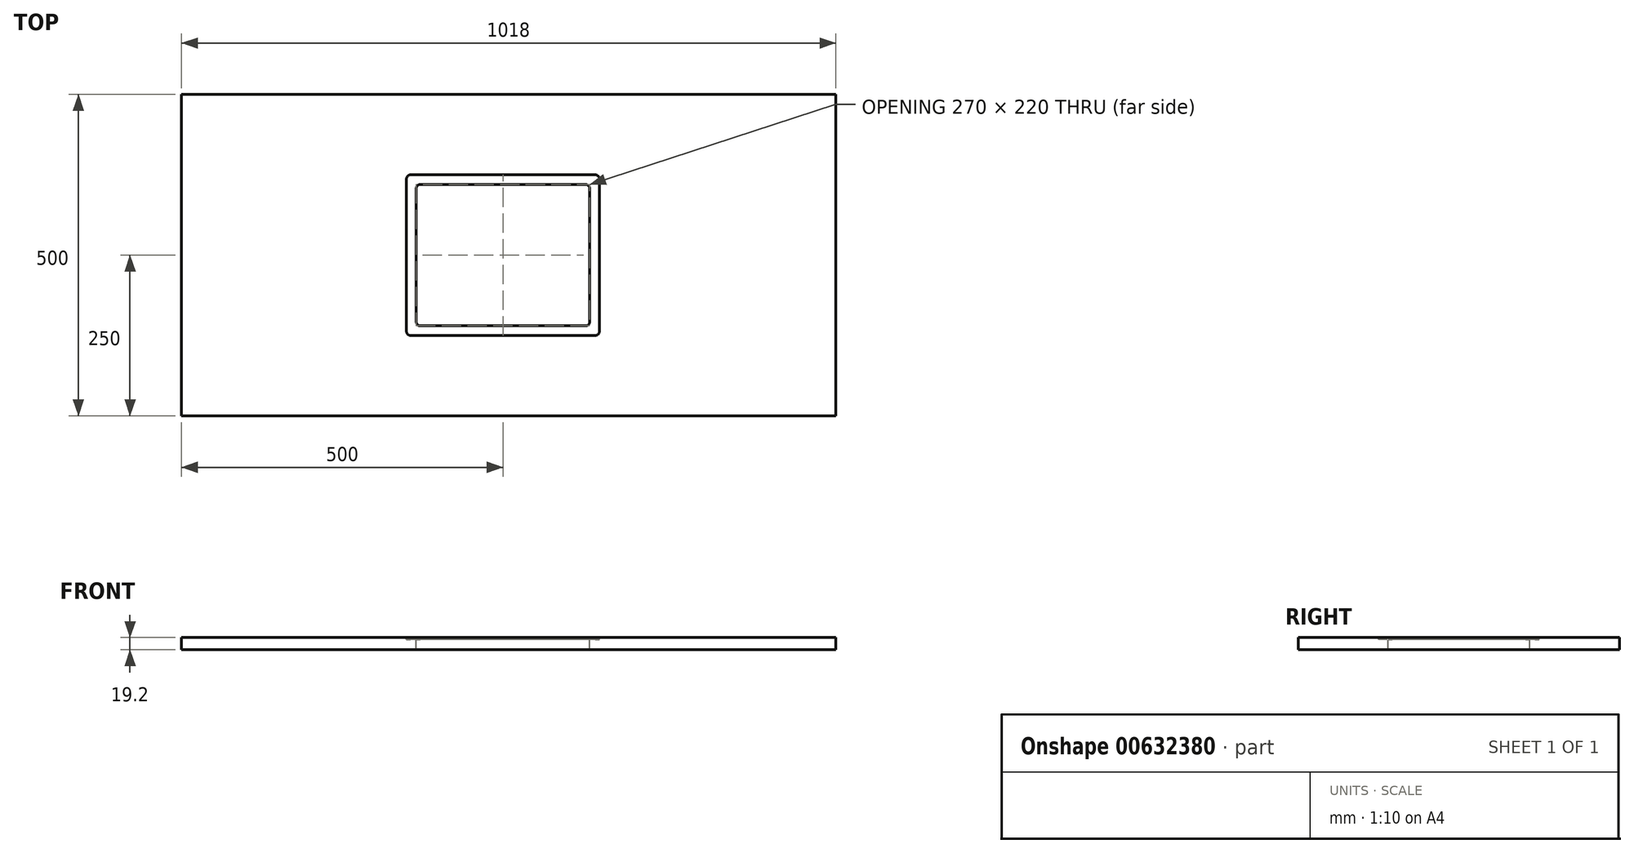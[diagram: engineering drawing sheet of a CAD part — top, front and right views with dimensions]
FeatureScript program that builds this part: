
annotation { "Feature Type Name" : "Feature", "Feature Type Description" : "" }
export const myFeature = defineFeature(function(context is Context, id is Id, definition is map)
    precondition{}
    {
        {
            var Q0;
            Q0=qCreatedBy(makeId("Top.planeOp"),FACE);
            var sketch = newSketch(context, id + "F0", { "sketchPlane" : qUnion([Q0])});
            skLineSegment(sketch, "E0.bottom", {"start": v(518, -250) * mm, "end": v(-500, -250) * mm});
            skLineSegment(sketch, "E0.top", {"start": v(518, 250) * mm, "end": v(-500, 250) * mm});
            skLineSegment(sketch, "E0.left", {"start": v(518, -250) * mm, "end": v(518, 250) * mm});
            skLineSegment(sketch, "E0.right", {"start": v(-500, -250) * mm, "end": v(-500, 250) * mm});
            skPoint(sketch, "E1", {"position": v(-500, 0) * mm});
            skSolve(sketch);
        }
        {
            var Q0;
            Q0 = qSketchRegion(id + "F0", true);
            extrude(context, id + "F1", {"entities" : qUnion([Q0]), "depth" : 19.2 * mm, "offsetDistance" : 25 * mm});
        }
        {
            var Q0;
            Q0=makeQuery(id+"F1.opExtrude","CAP_FACE",FACE,{"disambiguationData":[OSD([sQuery(id+"F0.wireOp",EDGE,"E0.bottom"),sQuery(id+"F0.wireOp",EDGE,"E0.top"),sQuery(id+"F0.wireOp",EDGE,"E0.left"),sQuery(id+"F0.wireOp",EDGE,"E0.right")])],"isStart":false});
            var sketch = newSketch(context, id + "F2", { "sketchPlane" : qUnion([Q0])});
            skLineSegment(sketch, "E2.bottom", {"start": v(143.65, 125) * mm, "end": v(-143.65, 125) * mm});
            skLineSegment(sketch, "E2.top", {"start": v(143.65, -125) * mm, "end": v(-143.65, -125) * mm});
            skLineSegment(sketch, "E2.left", {"start": v(150, 118.65) * mm, "end": v(150, -118.65) * mm});
            skLineSegment(sketch, "E2.right", {"start": v(-150, 118.65) * mm, "end": v(-150, -118.65) * mm});
            skPoint(sketch, "E2.middle", {"position": v(0, 0) * mm});
            skPoint(sketch, "E3.visualSharp", {"position": v(-150, 125) * mm});
            skArc(sketch, "E3.filletArc", {"start": v(-143.65, 125) * mm, "mid": v(-148.14, 123.14) * mm, "end": v(-150, 118.65) * mm});
            skPoint(sketch, "E4.visualSharp", {"position": v(-150, -125) * mm});
            skArc(sketch, "E4.filletArc", {"start": v(-150, -118.65) * mm, "mid": v(-148.14, -123.14) * mm, "end": v(-143.65, -125) * mm});
            skPoint(sketch, "E5.visualSharp", {"position": v(150, -125) * mm});
            skArc(sketch, "E5.filletArc", {"start": v(143.65, -125) * mm, "mid": v(148.14, -123.14) * mm, "end": v(150, -118.65) * mm});
            skPoint(sketch, "E6.visualSharp", {"position": v(150, 125) * mm});
            skArc(sketch, "E6.filletArc", {"start": v(150, 118.65) * mm, "mid": v(148.14, 123.14) * mm, "end": v(143.65, 125) * mm});
            skLineSegment(sketch, "E7.0", {"start": v(-135, 103.65) * mm, "end": v(-135, -103.65) * mm});
            skLineSegment(sketch, "E7.1", {"start": v(128.65, 110) * mm, "end": v(-128.65, 110) * mm});
            skLineSegment(sketch, "E7.2", {"start": v(135, 103.65) * mm, "end": v(135, -103.65) * mm});
            skLineSegment(sketch, "E7.3", {"start": v(128.65, -110) * mm, "end": v(-128.65, -110) * mm});
            skPoint(sketch, "E8.visualSharp", {"position": v(-135, 110) * mm});
            skArc(sketch, "E8.filletArc", {"start": v(-128.65, 110) * mm, "mid": v(-133.14, 108.14) * mm, "end": v(-135, 103.65) * mm});
            skPoint(sketch, "E9.visualSharp", {"position": v(135, 110) * mm});
            skArc(sketch, "E9.filletArc", {"start": v(135, 103.65) * mm, "mid": v(133.14, 108.14) * mm, "end": v(128.65, 110) * mm});
            skPoint(sketch, "E10.visualSharp", {"position": v(135, -110) * mm});
            skArc(sketch, "E10.filletArc", {"start": v(128.65, -110) * mm, "mid": v(133.14, -108.14) * mm, "end": v(135, -103.65) * mm});
            skPoint(sketch, "E11.visualSharp", {"position": v(-135, -110) * mm});
            skArc(sketch, "E11.filletArc", {"start": v(-135, -103.65) * mm, "mid": v(-133.14, -108.14) * mm, "end": v(-128.65, -110) * mm});
            skSolve(sketch);
        }
        {
            var Q0;
            Q0 = qSketchRegion(id + "F2", true);
            extrude(context, id + "F3", {"entities" : qUnion([Q0]), "operationType" : NewBodyOperationType.REMOVE, "oppositeDirection" : true, "depth" : 3 * mm, "offsetDistance" : 25 * mm});
        }
        {
            var Q0;
            Q0=makeQuery(id+"F2.imprint","IMPRINT",FACE,{"disambiguationData":[TD([[makeQuery(id+"F2.imprint","IMPRINT",EDGE,{"derivedFrom":sQuery(id+"F2.wireOp",EDGE,"E7.0")}),1.0]])]});
            extrude(context, id + "F4", {"entities" : qUnion([Q0]), "operationType" : NewBodyOperationType.REMOVE, "endBound" : BoundingType.UP_TO_NEXT, "oppositeDirection" : true, "depth" : 25 * mm, "offsetDistance" : 25 * mm});
        }
    });
